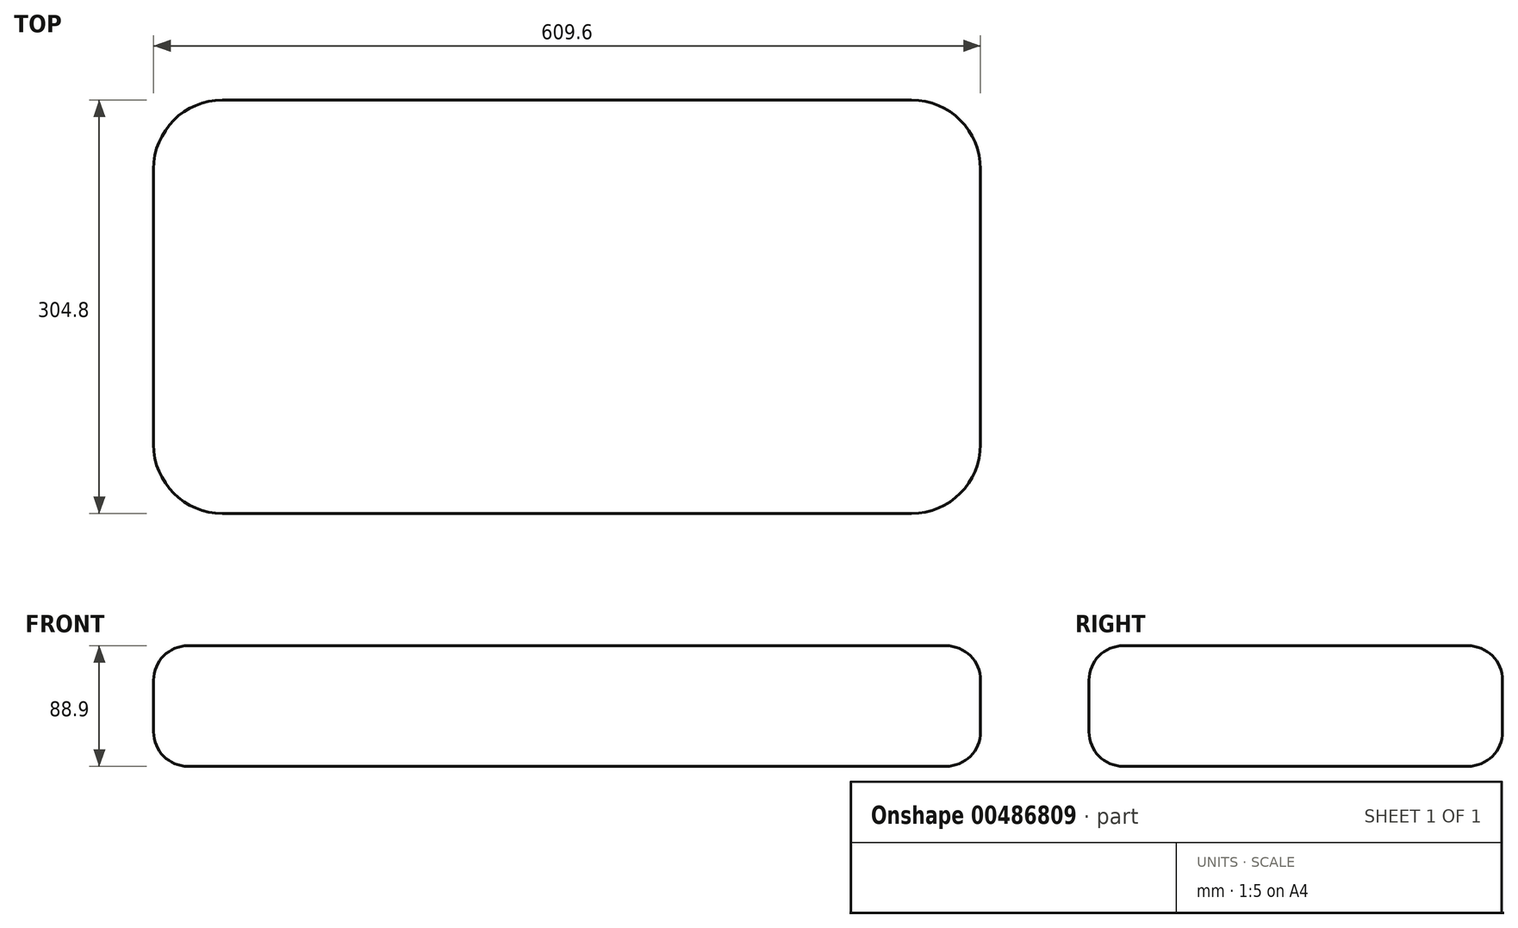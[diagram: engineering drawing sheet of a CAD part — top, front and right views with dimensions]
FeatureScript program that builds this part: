
annotation { "Feature Type Name" : "Feature", "Feature Type Description" : "" }
export const myFeature = defineFeature(function(context is Context, id is Id, definition is map)
    precondition{}
    {
        {
            var Q0;
            Q0=qCreatedBy(makeId("Top.planeOp"),FACE);
            var sketch = newSketch(context, id + "F0", { "sketchPlane" : qUnion([Q0])});
            skLineSegment(sketch, "E0.bottom", {"start": v(304.8, -152.4) * mm, "end": v(-304.8, -152.4) * mm});
            skLineSegment(sketch, "E0.top", {"start": v(304.8, 152.4) * mm, "end": v(-304.8, 152.4) * mm});
            skLineSegment(sketch, "E0.left", {"start": v(304.8, -152.4) * mm, "end": v(304.8, 152.4) * mm});
            skLineSegment(sketch, "E0.right", {"start": v(-304.8, -152.4) * mm, "end": v(-304.8, 152.4) * mm});
            skPoint(sketch, "E0.middle", {"position": v(0, 0) * mm});
            skSolve(sketch);
        }
        {
            var Q0;
            Q0=makeQuery(id+"F0.imprint","IMPRINT",FACE,{"disambiguationData":[TD([[makeQuery(id+"F0.imprint","IMPRINT",EDGE,{"derivedFrom":sQuery(id+"F0.wireOp",EDGE,"E0.bottom")}),-1.0]])]});
            extrude(context, id + "F1", {"entities" : qUnion([Q0]), "depth" : 88.9 * mm, "offsetDistance" : 25.4 * mm});
        }
        {
            var Q0;
            Q0=makeQuery(id+"F1.opExtrude","SWEPT_EDGE",EDGE,{"disambiguationData":[OSD([sQuery(id+"F0.wireOp",EDGE,"E0.top"),sQuery(id+"F0.wireOp",EDGE,"E0.right")])]});
            var Q1;
            Q1=makeQuery(id+"F1.opExtrude","SWEPT_EDGE",EDGE,{"disambiguationData":[OSD([sQuery(id+"F0.wireOp",EDGE,"E0.bottom"),sQuery(id+"F0.wireOp",EDGE,"E0.right")])]});
            var Q2;
            Q2=makeQuery(id+"F1.opExtrude","SWEPT_EDGE",EDGE,{"disambiguationData":[OSD([sQuery(id+"F0.wireOp",EDGE,"E0.bottom"),sQuery(id+"F0.wireOp",EDGE,"E0.left")])]});
            var Q3;
            Q3=makeQuery(id+"F1.opExtrude","SWEPT_EDGE",EDGE,{"disambiguationData":[OSD([sQuery(id+"F0.wireOp",EDGE,"E0.top"),sQuery(id+"F0.wireOp",EDGE,"E0.left")])]});
            fillet(context, id + "F2", {"entities" : qUnion([Q0, Q1, Q2, Q3]), "radius" : 50.8 * mm, "tangentPropagation" : true, "allowEdgeOverflow" : false});
        }
        {
            var Q0;
            Q0=makeQuery(id+"F1.opExtrude","CAP_EDGE",EDGE,{"disambiguationData":[OSD([sQuery(id+"F0.wireOp",EDGE,"E0.bottom")])],"isStart":false});
            var Q1;
            Q1=makeQuery(id+"F1.opExtrude","CAP_EDGE",EDGE,{"disambiguationData":[OSD([sQuery(id+"F0.wireOp",EDGE,"E0.top")])],"isStart":false});
            var Q2;
            Q2=makeQuery(id+"F1.opExtrude","CAP_EDGE",EDGE,{"disambiguationData":[OSD([sQuery(id+"F0.wireOp",EDGE,"E0.top")])],"isStart":true});
            fillet(context, id + "F3", {"entities" : qUnion([Q0, Q1, Q2]), "radius" : 25.4 * mm, "tangentPropagation" : true, "allowEdgeOverflow" : false});
        }
    });
